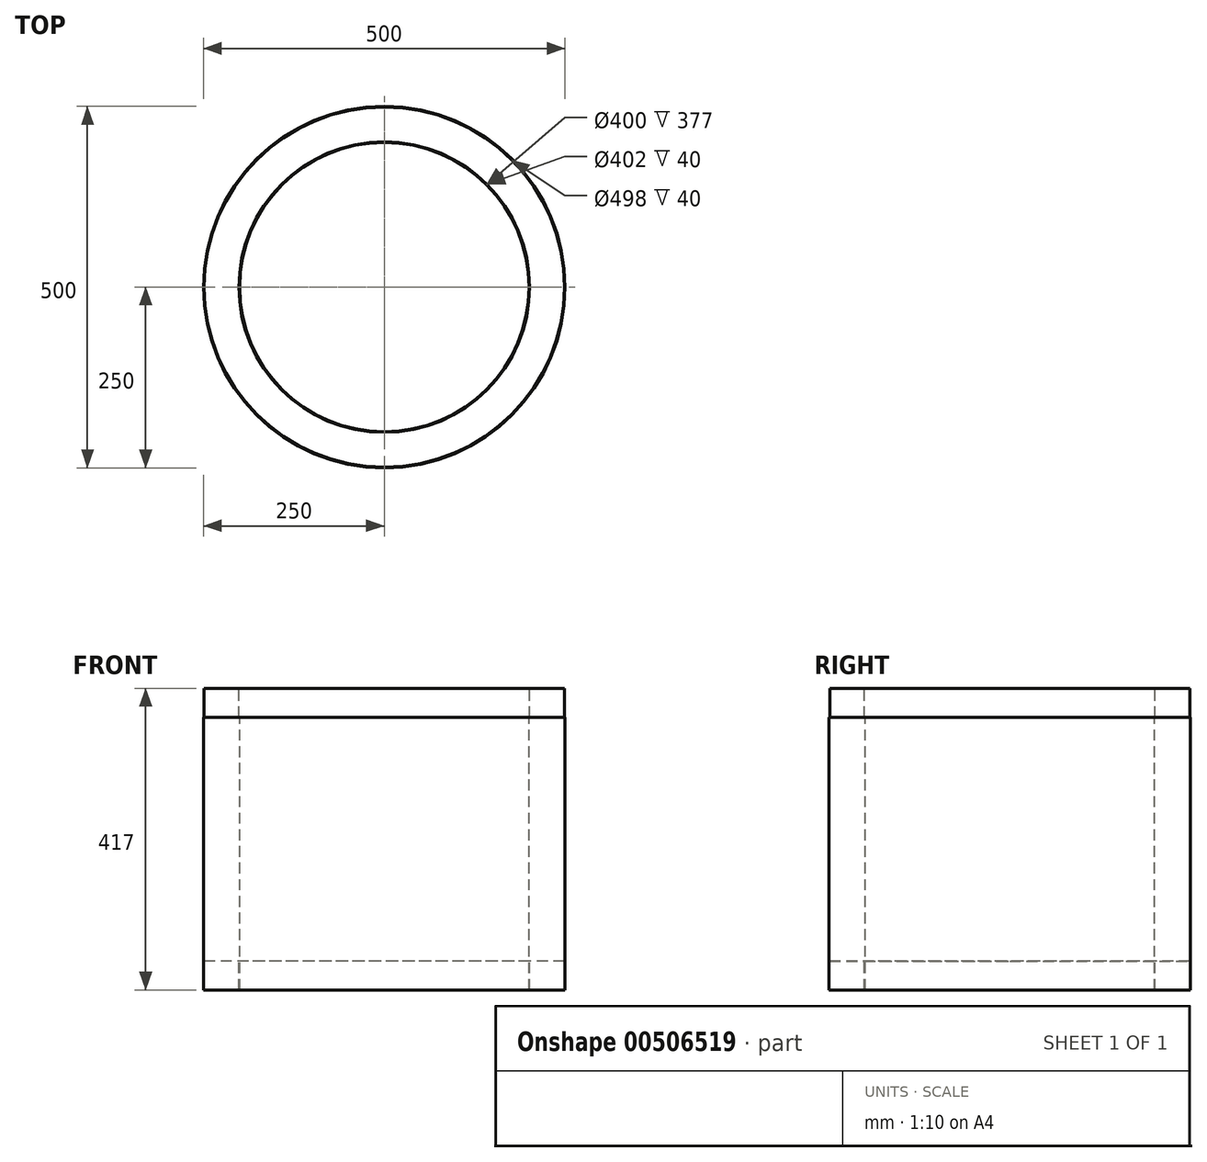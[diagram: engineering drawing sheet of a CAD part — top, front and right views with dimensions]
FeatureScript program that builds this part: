
annotation { "Feature Type Name" : "Feature", "Feature Type Description" : "" }
export const myFeature = defineFeature(function(context is Context, id is Id, definition is map)
    precondition{}
    {
        {
            var Q0;
            Q0=qCreatedBy(makeId("Front.planeOp"),FACE);
            var sketch = newSketch(context, id + "F0", { "sketchPlane" : qUnion([Q0])});
            skLineSegment(sketch, "E0", {"start": v(0, 74.87) * mm, "end": v(0, -73.71) * mm, "construction": true});
            skLineSegment(sketch, "E1", {"start": v(0, 374.84) * mm, "end": v(0, -528.94) * mm, "construction": true});
            skLineSegment(sketch, "E2", {"start": v(-200, -489.75) * mm, "end": v(-200, -112.75) * mm});
            skLineSegment(sketch, "E3", {"start": v(-200, -112.75) * mm, "end": v(-201, -112.75) * mm});
            skLineSegment(sketch, "E4", {"start": v(-201, -112.75) * mm, "end": v(-201, -72.75) * mm});
            skLineSegment(sketch, "E5", {"start": v(-201, -72.75) * mm, "end": v(-249, -72.75) * mm});
            skLineSegment(sketch, "E6", {"start": v(-249, -72.75) * mm, "end": v(-249, -112.75) * mm});
            skLineSegment(sketch, "E7", {"start": v(-249, -112.75) * mm, "end": v(-250, -112.75) * mm});
            skLineSegment(sketch, "E8", {"start": v(-250, -112.75) * mm, "end": v(-250, -489.75) * mm});
            skLineSegment(sketch, "E9", {"start": v(-250, -489.75) * mm, "end": v(-249, -489.75) * mm});
            skLineSegment(sketch, "E10", {"start": v(-249, -489.75) * mm, "end": v(-249, -449.75) * mm});
            skLineSegment(sketch, "E11", {"start": v(-249, -449.75) * mm, "end": v(-201, -449.75) * mm});
            skLineSegment(sketch, "E12", {"start": v(-201, -449.75) * mm, "end": v(-201, -489.75) * mm});
            skLineSegment(sketch, "E13", {"start": v(-201, -489.75) * mm, "end": v(-200, -489.75) * mm});
            skSolve(sketch);
        }
        {
            var Q0;
            Q0=qSketchRegion(id+"F0",true);
            var Q1;
            Q1=sQuery(id+"F0.wireOp",EDGE,"E1");
            revolve(context, id + "F1", {"entities" : qUnion([Q0]), "axis" : qUnion([Q1]), "revolveType" : RevolveType.FULL});
        }
    });
